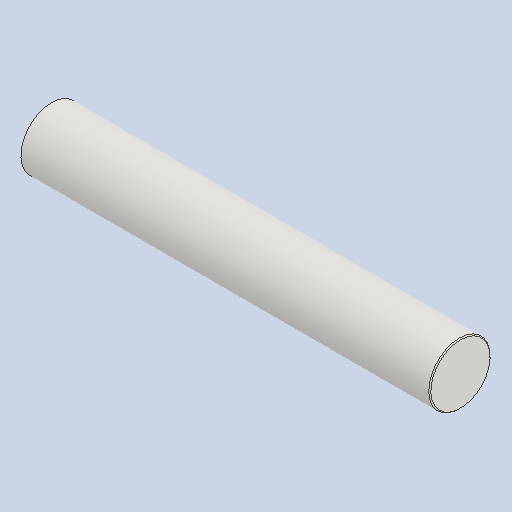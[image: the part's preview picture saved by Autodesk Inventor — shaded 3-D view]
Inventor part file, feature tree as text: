
AUTODESK INVENTOR PART (.ipt)
format: ipt  version: 2022 (Build 260153000, 153)  size: 89,088 bytes
history: native  units: mm
features: other x3, revolve x1, chamfer x1
ambient origin geometry x6: Origin, XZ Plane, XY Plane, X Axis, Y Axis, Z Axis
bodies: Solid1 (feature_tree)
feature tree (5):
  revolve  "Revolution1"  [1 undecoded]
  chamfer  "Chamfer1"  Distance=6.0mm
  other  "Start Plane"
  other  "Origin point"
  other  "Main Sketch"
note: 1 required parameter value undecoded (feature->parameter linkage not recoverable at this tier; creation-order binding heuristic only, values carry confidence <= 0.55)
